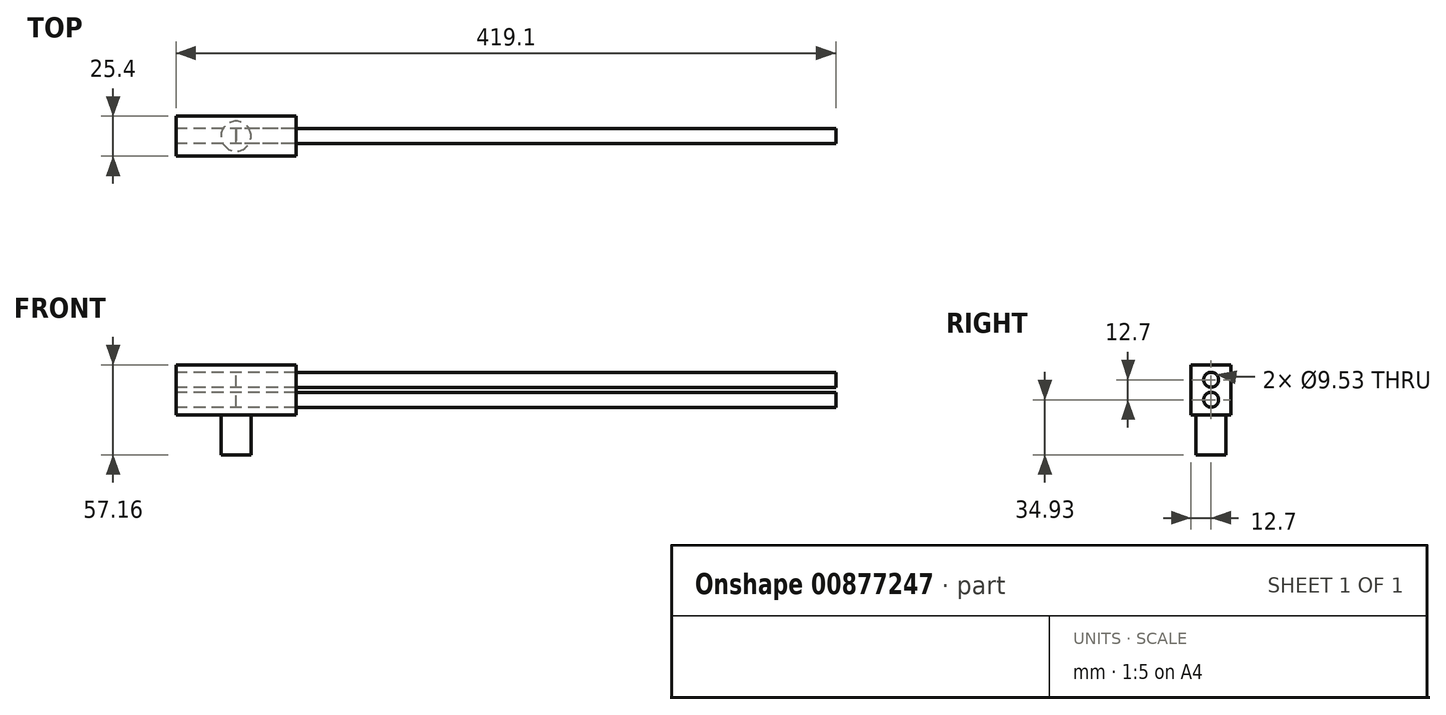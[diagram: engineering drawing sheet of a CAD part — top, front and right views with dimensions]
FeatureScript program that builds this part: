
annotation { "Feature Type Name" : "Feature", "Feature Type Description" : "" }
export const myFeature = defineFeature(function(context is Context, id is Id, definition is map)
    precondition{}
    {
        {
            var Q0;
            Q0=qCreatedBy(makeId("Right.planeOp"),FACE);
            var sketch = newSketch(context, id + "F0", { "sketchPlane" : qUnion([Q0])});
            skCircle(sketch, "E0", {"center": v(0, 6.35) * mm, "radius": 4.76 * mm});
            skCircle(sketch, "E1", {"center": v(0, -6.35) * mm, "radius": 4.76 * mm});
            skLineSegment(sketch, "E2.bottom", {"start": v(-12.7, 15.88) * mm, "end": v(12.7, 15.87) * mm});
            skLineSegment(sketch, "E2.top", {"start": v(-12.7, -15.88) * mm, "end": v(12.7, -15.88) * mm});
            skLineSegment(sketch, "E2.left", {"start": v(-12.7, 15.88) * mm, "end": v(-12.7, -15.88) * mm});
            skLineSegment(sketch, "E2.right", {"start": v(12.7, 15.88) * mm, "end": v(12.7, -15.88) * mm});
            skSolve(sketch);
        }
        {
            var Q0;
            Q0 = qSketchRegion(id + "F0", true);
            extrude(context, id + "F1", {"entities" : qUnion([Q0]), "depth" : 76.2 * mm, "offsetDistance" : 25.4 * mm, "symmetric" : true});
        }
        {
            var Q0;
            Q0=makeQuery(id+"F0.imprint","IMPRINT",FACE,{"disambiguationData":[TD([[makeQuery(id+"F0.imprint","IMPRINT",EDGE,{"derivedFrom":sQuery(id+"F0.wireOp",EDGE,"E0")}),1.0]])]});
            var Q1;
            Q1=makeQuery(id+"F0.imprint","IMPRINT",FACE,{"disambiguationData":[TD([[makeQuery(id+"F0.imprint","IMPRINT",EDGE,{"derivedFrom":sQuery(id+"F0.wireOp",EDGE,"E1")}),1.0]])]});
            extrude(context, id + "F2", {"entities" : qUnion([Q0, Q1]), "depth" : 381 * mm, "offsetDistance" : 25.4 * mm});
        }
        {
            var Q0;
            Q0=makeQuery(id+"F1.opExtrude","SWEPT_FACE",FACE,{"disambiguationData":[OSD([sQuery(id+"F0.wireOp",EDGE,"E2.top")])]});
            var sketch = newSketch(context, id + "F3", { "sketchPlane" : qUnion([Q0])});
            skCircle(sketch, "E3", {"center": v(0, 0) * mm, "radius": 9.53 * mm});
            skLineSegment(sketch, "E4.0", {"start": v(38.1, 12.7) * mm, "end": v(38.1, -12.7) * mm});
            skLineSegment(sketch, "E5.0", {"start": v(-38.1, 12.7) * mm, "end": v(-38.1, -12.7) * mm});
            skSolve(sketch);
        }
        {
            var Q0;
            Q0 = qSketchRegion(id + "F3", true);
            extrude(context, id + "F4", {"entities" : qUnion([Q0]), "operationType" : NewBodyOperationType.ADD, "depth" : 25.4 * mm, "offsetDistance" : 25.4 * mm});
        }
    });
